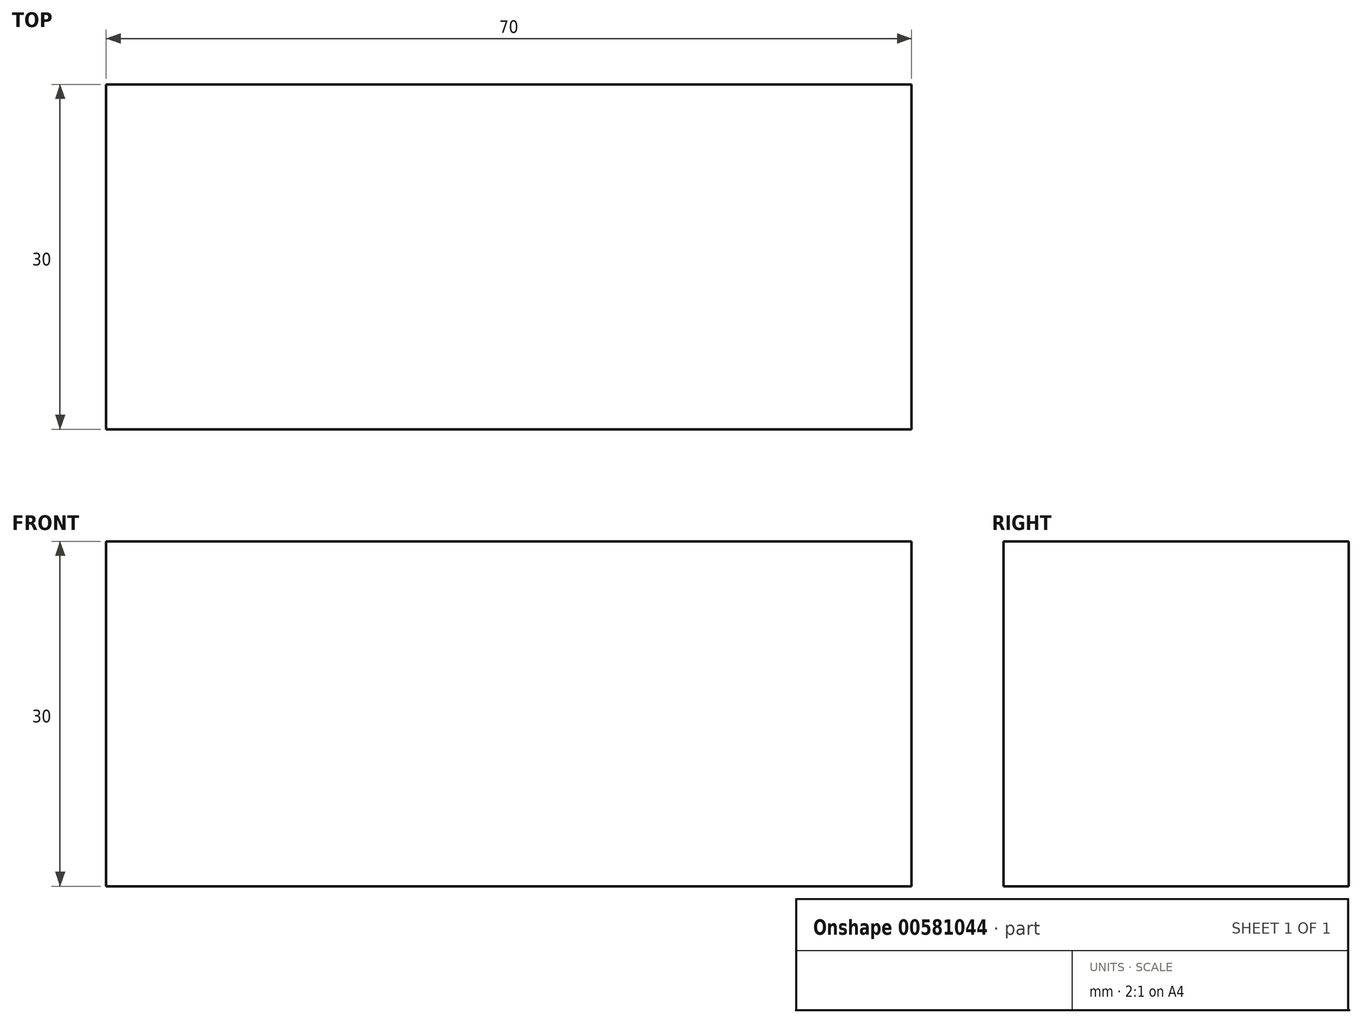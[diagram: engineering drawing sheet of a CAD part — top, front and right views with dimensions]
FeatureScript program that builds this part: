
annotation { "Feature Type Name" : "Feature", "Feature Type Description" : "" }
export const myFeature = defineFeature(function(context is Context, id is Id, definition is map)
    precondition{}
    {
        {
            var Q0;
            Q0=qCreatedBy(makeId("Top.planeOp"),FACE);
            var sketch = newSketch(context, id + "F0", { "sketchPlane" : qUnion([Q0])});
            skLineSegment(sketch, "E0.bottom", {"start": v(-35, -15) * mm, "end": v(35, -15) * mm});
            skLineSegment(sketch, "E0.top", {"start": v(-35, 15) * mm, "end": v(35, 15) * mm});
            skLineSegment(sketch, "E0.left", {"start": v(-35, -15) * mm, "end": v(-35, 15) * mm});
            skLineSegment(sketch, "E0.right", {"start": v(35, -15) * mm, "end": v(35, 15) * mm});
            skPoint(sketch, "E0.middle", {"position": v(0, 0) * mm});
            skSolve(sketch);
        }
        {
            var Q0;
            Q0 = qSketchRegion(id + "F0", true);
            extrude(context, id + "F1", {"entities" : qUnion([Q0]), "endBound" : BoundingType.SYMMETRIC, "depth" : 30 * mm, "offsetDistance" : 25 * mm});
        }
    });
